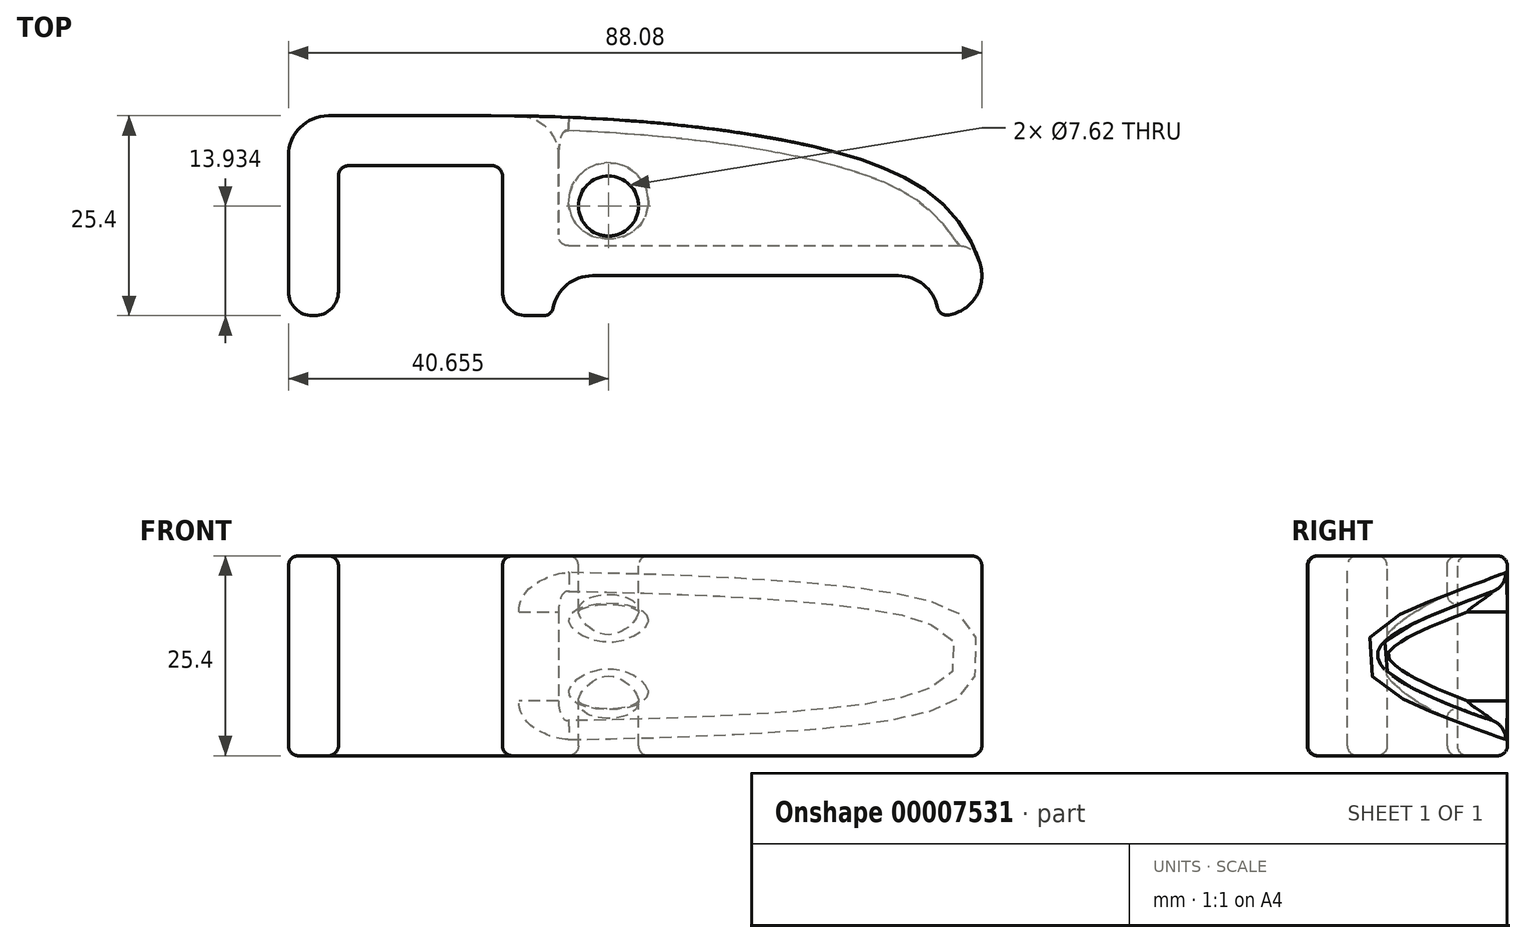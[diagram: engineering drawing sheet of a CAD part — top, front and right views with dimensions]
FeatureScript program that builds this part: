
annotation { "Feature Type Name" : "Feature", "Feature Type Description" : "" }
export const myFeature = defineFeature(function(context is Context, id is Id, definition is map)
    precondition{}
    {
        {
            var Q0;
            Q0=qCreatedBy(makeId("Top.planeOp"),FACE);
            var sketch = newSketch(context, id + "F0", { "sketchPlane" : qUnion([Q0])});
            skLineSegment(sketch, "E0", {"start": v(0, 0) * mm, "end": v(0, -25.4) * mm});
            skLineSegment(sketch, "E1", {"start": v(0, -25.4) * mm, "end": v(6.35, -25.4) * mm});
            skLineSegment(sketch, "E2", {"start": v(6.35, -25.4) * mm, "end": v(6.35, -6.35) * mm});
            skLineSegment(sketch, "E3", {"start": v(6.35, -6.35) * mm, "end": v(27.18, -6.35) * mm});
            skLineSegment(sketch, "E4", {"start": v(27.18, -6.35) * mm, "end": v(27.18, -25.4) * mm});
            skLineSegment(sketch, "E5", {"start": v(27.18, -25.4) * mm, "end": v(88.9, -25.4) * mm});
            skLineSegment(sketch, "E6", {"start": v(88.9, -25.4) * mm, "end": v(88.9, 0) * mm});
            skLineSegment(sketch, "E7", {"start": v(88.9, 0) * mm, "end": v(0, 0) * mm});
            skFitSpline(sketch, "E8", {"points": [v(25.73, 0) * mm, v(69.73, -4.7) * mm, v(84.63, -12.83) * mm, v(88.9, -25.4) * mm], "startDerivative": vector(108.81, 0) * mm, "endDerivative": vector(0, -54) * mm});
            skSolve(sketch);
        }
        {
            var Q0;
            {var subQ2=sQuery(id+"F0.wireOp",EDGE,"E0");Q0=makeQuery(id+"F0.imprint","IMPRINT",FACE,{"disambiguationData":[TD([[makeQuery(id+"F0.imprint","IMPRINT",EDGE,{"derivedFrom":subQ2}),1.0]])]});}
            extrude(context, id + "F1", {"entities" : qUnion([Q0]), "depth" : 25.4 * mm});
        }
        {
            var Q0;
            Q0=makeQuery(id+"F1.opExtrude","CAP_VERTEX",VERTEX,{"disambiguationData":[OSD([sQuery(id+"F0.wireOp",EDGE,"E5"),sQuery(id+"F0.wireOp",EDGE,"E6"),sQuery(id+"F0.wireOp",EDGE,"E8")])],"isStart":false});
            var Q1;
            Q1=qCreatedBy(makeId("Right.planeOp"),FACE);
            cPlane(context, id + "F2", {"entities" : qUnion([Q0, Q1]), "cplaneType" : CPlaneType.PLANE_POINT, "offset" : 152.4 * mm, "width" : 152.4 * mm, "height" : 152.4 * mm});
        }
        {
            var Q0;
            Q0=qCreatedBy(id+"F2.planeOp",FACE);
            var sketch = newSketch(context, id + "F3", { "sketchPlane" : qUnion([Q0])});
            skLineSegment(sketch, "E9.0.1", {"start": v(0, 0) * mm, "end": v(0, 25.4) * mm});
            skLineSegment(sketch, "E9.0.3", {"start": v(-25.4, 25.4) * mm, "end": v(-25.4, 0) * mm});
            skFitSpline(sketch, "E10", {"points": [v(0, 21.6) * mm, v(-16.51, 12.7) * mm, v(0, 3.81) * mm], "startDerivative": vector(-56.73, -21.7) * mm, "endDerivative": vector(53.72, -18.15) * mm});
            skLineSegment(sketch, "E11", {"start": v(0, 12.7) * mm, "end": v(-16.51, 12.7) * mm, "construction": true});
            skSolve(sketch);
        }
        {
            var Q0;
            Q0 = qSketchRegion(id + "F3", true);
            extrude(context, id + "F4", {"entities" : qUnion([Q0]), "operationType" : NewBodyOperationType.REMOVE, "oppositeDirection" : true, "depth" : 54.6 * mm});
        }
        {
            var Q0;
            Q0=makeQuery(id+"F1.opExtrude","CAP_FACE",FACE,{"disambiguationData":[OSD([sQuery(id+"F0.wireOp",EDGE,"E0"),sQuery(id+"F0.wireOp",EDGE,"E1"),sQuery(id+"F0.wireOp",EDGE,"E2"),sQuery(id+"F0.wireOp",EDGE,"E3"),sQuery(id+"F0.wireOp",EDGE,"E4"),sQuery(id+"F0.wireOp",EDGE,"E5"),sQuery(id+"F0.wireOp",EDGE,"E7"),sQuery(id+"F0.wireOp",EDGE,"E8")])],"isStart":false});
            var sketch = newSketch(context, id + "F5", { "sketchPlane" : qUnion([Q0])});
            skCircle(sketch, "E12", {"center": v(40.66, -11.47) * mm, "radius": 3.81 * mm});
            skSolve(sketch);
        }
        {
            var Q0;
            Q0 = qSketchRegion(id + "F5", true);
            extrude(context, id + "F6", {"entities" : qUnion([Q0]), "operationType" : NewBodyOperationType.REMOVE, "endBound" : BoundingType.THROUGH_ALL, "oppositeDirection" : true, "depth" : 25.4 * mm});
        }
        {
            var Q0;
            Q0=makeQuery(id+"F1.opExtrude","CAP_FACE",FACE,{"disambiguationData":[OSD([sQuery(id+"F0.wireOp",EDGE,"E0"),sQuery(id+"F0.wireOp",EDGE,"E1"),sQuery(id+"F0.wireOp",EDGE,"E2"),sQuery(id+"F0.wireOp",EDGE,"E3"),sQuery(id+"F0.wireOp",EDGE,"E4"),sQuery(id+"F0.wireOp",EDGE,"E5"),sQuery(id+"F0.wireOp",EDGE,"E7"),sQuery(id+"F0.wireOp",EDGE,"E8")])],"isStart":false});
            var sketch = newSketch(context, id + "F7", { "sketchPlane" : qUnion([Q0])});
            skLineSegment(sketch, "E13", {"start": v(82.55, -20.32) * mm, "end": v(33.53, -20.32) * mm});
            skLineSegment(sketch, "E14", {"start": v(33.53, -20.32) * mm, "end": v(33.53, -25.4) * mm});
            skLineSegment(sketch, "E15", {"start": v(82.55, -20.32) * mm, "end": v(82.55, -25.4) * mm});
            skSolve(sketch);
        }
        {
            var Q0;
            Q0 = qSketchRegion(id + "F7", true);
            var Q1;
            Q1=makeQuery(id+"F7.imprint","IMPRINT",FACE,{"disambiguationData":[TD([[makeQuery(id+"F7.imprint","IMPRINT",EDGE,{"derivedFrom":sQuery(id+"F7.wireOp",EDGE,"E13")}),1.0]])]});
            extrude(context, id + "F8", {"entities" : qUnion([Q0, Q1]), "operationType" : NewBodyOperationType.REMOVE, "endBound" : BoundingType.THROUGH_ALL, "oppositeDirection" : true, "depth" : 25.4 * mm});
        }
        {
            var Q0;
            Q0=makeQuery(id+"F4.boolean.opBoolean","INTERSECT",EDGE,{"derivedFrom":[makeQuery(id+"F1.opExtrude","SWEPT_FACE",FACE,{"disambiguationData":[OSD([sQuery(id+"F0.wireOp",EDGE,"E8")])]}),makeQuery(id+"F4.opExtrude","SWEPT_FACE",FACE,{"disambiguationData":[OSD([sQuery(id+"F3.wireOp",EDGE,"E10")])]})]});
            fillet(context, id + "F9", {"entities" : qUnion([Q0]), "radius" : 2.54 * mm, "tangentPropagation" : true, "allowEdgeOverflow" : false});
        }
        {
            var Q0;
            Q0=makeQuery(id+"F1.opExtrude","SWEPT_EDGE",EDGE,{"disambiguationData":[OSD([sQuery(id+"F0.wireOp",EDGE,"E5"),sQuery(id+"F0.wireOp",EDGE,"E6"),sQuery(id+"F0.wireOp",EDGE,"E8")])]});
            var Q1;
            Q1=makeQuery(id+"F1.opExtrude","SWEPT_EDGE",EDGE,{"disambiguationData":[OSD([sQuery(id+"F0.wireOp",EDGE,"E0"),sQuery(id+"F0.wireOp",EDGE,"E7")])]});
            fillet(context, id + "F10", {"entities" : qUnion([Q0, Q1]), "radius" : 5.08 * mm, "tangentPropagation" : true, "allowEdgeOverflow" : false});
        }
        {
            var Q0;
            Q0=makeQuery(id+"F1.opExtrude","SWEPT_EDGE",EDGE,{"disambiguationData":[OSD([sQuery(id+"F0.wireOp",EDGE,"E4"),sQuery(id+"F0.wireOp",EDGE,"E5")])]});
            var Q1;
            Q1=makeQuery(id+"F1.opExtrude","SWEPT_EDGE",EDGE,{"disambiguationData":[OSD([sQuery(id+"F0.wireOp",EDGE,"E1"),sQuery(id+"F0.wireOp",EDGE,"E2")])]});
            var Q2;
            Q2=makeQuery(id+"F1.opExtrude","SWEPT_EDGE",EDGE,{"disambiguationData":[OSD([sQuery(id+"F0.wireOp",EDGE,"E0"),sQuery(id+"F0.wireOp",EDGE,"E1")])]});
            fillet(context, id + "F11", {"entities" : qUnion([Q0, Q1, Q2]), "radius" : 3.05 * mm, "tangentPropagation" : true, "allowEdgeOverflow" : false});
        }
        {
            var Q0;
            Q0=makeQuery(id+"F4.boolean.opBoolean","COPY",EDGE,{"derivedFrom":makeQuery(id+"F4.opExtrude","CAP_EDGE",EDGE,{"disambiguationData":[OSD([sQuery(id+"F3.wireOp",EDGE,"E10")])],"isStart":false})});
            fillet(context, id + "F12", {"entities" : qUnion([Q0]), "radius" : 1.27 * mm, "tangentPropagation" : true, "allowEdgeOverflow" : false});
        }
        {
            var Q0;
            Q0=makeQuery(id+"F4.boolean.opBoolean","INTERSECT",EDGE,{"derivedFrom":[makeQuery(id+"F1.opExtrude","SWEPT_FACE",FACE,{"disambiguationData":[OSD([sQuery(id+"F0.wireOp",EDGE,"E8")])]}),makeQuery(id+"F4.opExtrude","CAP_FACE",FACE,{"disambiguationData":[OSD([sQuery(id+"F3.wireOp",EDGE,"E9.0.1"),sQuery(id+"F3.wireOp",EDGE,"E10")])],"isStart":false})]});
            fillet(context, id + "F13", {"entities" : qUnion([Q0]), "radius" : 5.08 * mm, "tangentPropagation" : true, "allowEdgeOverflow" : false});
        }
        {
            var Q0;
            Q0=makeQuery(id+"F1.opExtrude","SWEPT_EDGE",EDGE,{"disambiguationData":[OSD([sQuery(id+"F0.wireOp",EDGE,"E2"),sQuery(id+"F0.wireOp",EDGE,"E3")])]});
            var Q1;
            Q1=makeQuery(id+"F1.opExtrude","SWEPT_EDGE",EDGE,{"disambiguationData":[OSD([sQuery(id+"F0.wireOp",EDGE,"E3"),sQuery(id+"F0.wireOp",EDGE,"E4")])]});
            fillet(context, id + "F14", {"entities" : qUnion([Q0, Q1]), "radius" : 1.27 * mm, "tangentPropagation" : true, "allowEdgeOverflow" : false});
        }
        {
            var Q0;
            Q0=makeQuery(id+"F6.boolean.opBoolean","INTERSECT",EDGE,{"derivedFrom":[makeQuery(id+"F4.boolean.opBoolean","COPY",FACE,{"derivedFrom":makeQuery(id+"F4.opExtrude","SWEPT_FACE",FACE,{"disambiguationData":[OSD([sQuery(id+"F3.wireOp",EDGE,"E10")])]})}),makeQuery(id+"F6.opExtrude","SWEPT_FACE",FACE,{"disambiguationData":[OSD([sQuery(id+"F5.wireOp",EDGE,"E12")])]})]});
            fillet(context, id + "F15", {"entities" : qUnion([Q0]), "radius" : 1.27 * mm, "tangentPropagation" : true, "allowEdgeOverflow" : false});
        }
        {
            var Q0;
            Q0=makeQuery(id+"F8.boolean.opBoolean","COPY",EDGE,{"derivedFrom":makeQuery(id+"F8.opExtrude","SWEPT_EDGE",EDGE,{"disambiguationData":[OSD([sQuery(id+"F7.wireOp",EDGE,"E13"),sQuery(id+"F7.wireOp",EDGE,"E14")])]})});
            var Q1;
            Q1=makeQuery(id+"F8.boolean.opBoolean","COPY",EDGE,{"derivedFrom":makeQuery(id+"F8.opExtrude","SWEPT_EDGE",EDGE,{"disambiguationData":[OSD([sQuery(id+"F7.wireOp",EDGE,"E13"),sQuery(id+"F7.wireOp",EDGE,"E15")])]})});
            fillet(context, id + "F16", {"entities" : qUnion([Q0, Q1]), "radius" : 5.08 * mm, "tangentPropagation" : true, "allowEdgeOverflow" : false});
        }
        {
            var Q0;
            {var subQ0=sQuery(id+"F7.wireOp",EDGE,"E15");var subQ1=sQuery(id+"F0.wireOp",EDGE,"E5");var subQ2=sQuery(id+"F0.wireOp",EDGE,"E8");Q0=makeQuery(id+"F16.opFillet","BLEND_EDGE",EDGE,{"blendedFrom":[makeQuery(id+"F8.boolean.opBoolean","COPY",EDGE,{"derivedFrom":makeQuery(id+"F8.opExtrude","SWEPT_EDGE",EDGE,{"disambiguationData":[OSD([sQuery(id+"F7.wireOp",EDGE,"E13"),subQ0])]})}),makeQuery(id+"F8.boolean.opBoolean","SPLIT",FACE,{"disambiguationData":[TD([makeQuery(id+"F1.opExtrude","SWEPT_FACE",FACE,{"disambiguationData":[OSD([subQ2])]})])],"derivedFrom":makeQuery(id+"F1.opExtrude","SWEPT_FACE",FACE,{"disambiguationData":[OSD([subQ1])]})})],"blendedInto":[makeQuery(id+"F8.boolean.opBoolean","SPLIT",FACE,{"disambiguationData":[TD([makeQuery(id+"F1.opExtrude","SWEPT_FACE",FACE,{"disambiguationData":[OSD([subQ2])]})])],"derivedFrom":makeQuery(id+"F1.opExtrude","SWEPT_FACE",FACE,{"disambiguationData":[OSD([subQ1])]})})]});}
            var Q1;
            {var subQ0=sQuery(id+"F7.wireOp",EDGE,"E14");var subQ1=sQuery(id+"F0.wireOp",EDGE,"E5");var subQ2=sQuery(id+"F0.wireOp",EDGE,"E4");Q1=makeQuery(id+"F16.opFillet","BLEND_EDGE",EDGE,{"blendedFrom":[makeQuery(id+"F8.boolean.opBoolean","COPY",EDGE,{"derivedFrom":makeQuery(id+"F8.opExtrude","SWEPT_EDGE",EDGE,{"disambiguationData":[OSD([sQuery(id+"F7.wireOp",EDGE,"E13"),subQ0])]})}),makeQuery(id+"F8.boolean.opBoolean","SPLIT",FACE,{"disambiguationData":[TD([makeQuery(id+"F1.opExtrude","SWEPT_FACE",FACE,{"disambiguationData":[OSD([subQ2])]})])],"derivedFrom":makeQuery(id+"F1.opExtrude","SWEPT_FACE",FACE,{"disambiguationData":[OSD([subQ1])]})})],"blendedInto":[makeQuery(id+"F8.boolean.opBoolean","SPLIT",FACE,{"disambiguationData":[TD([makeQuery(id+"F1.opExtrude","SWEPT_FACE",FACE,{"disambiguationData":[OSD([subQ2])]})])],"derivedFrom":makeQuery(id+"F1.opExtrude","SWEPT_FACE",FACE,{"disambiguationData":[OSD([subQ1])]})})]});}
            fillet(context, id + "F17", {"entities" : qUnion([Q0, Q1]), "radius" : 1.27 * mm, "tangentPropagation" : true, "allowEdgeOverflow" : false});
        }
        {
            var Q0;
            Q0=makeQuery(id+"F1.opExtrude","CAP_FACE",FACE,{"disambiguationData":[OSD([sQuery(id+"F0.wireOp",EDGE,"E0"),sQuery(id+"F0.wireOp",EDGE,"E1"),sQuery(id+"F0.wireOp",EDGE,"E2"),sQuery(id+"F0.wireOp",EDGE,"E3"),sQuery(id+"F0.wireOp",EDGE,"E4"),sQuery(id+"F0.wireOp",EDGE,"E5"),sQuery(id+"F0.wireOp",EDGE,"E7"),sQuery(id+"F0.wireOp",EDGE,"E8")])],"isStart":false});
            var Q1;
            Q1=makeQuery(id+"F1.opExtrude","CAP_FACE",FACE,{"disambiguationData":[OSD([sQuery(id+"F0.wireOp",EDGE,"E0"),sQuery(id+"F0.wireOp",EDGE,"E1"),sQuery(id+"F0.wireOp",EDGE,"E2"),sQuery(id+"F0.wireOp",EDGE,"E3"),sQuery(id+"F0.wireOp",EDGE,"E4"),sQuery(id+"F0.wireOp",EDGE,"E5"),sQuery(id+"F0.wireOp",EDGE,"E7"),sQuery(id+"F0.wireOp",EDGE,"E8")])],"isStart":true});
            fillet(context, id + "F18", {"entities" : qUnion([Q0, Q1]), "radius" : 1.27 * mm, "tangentPropagation" : true, "allowEdgeOverflow" : false});
        }
    });
